# Revit family: Haworth_XSeries_LateralFile
name_source: partatom
category: Furniture Systems
revit_build: Autodesk Revit 2018 (Build: 20170223_1515(x64)
units: mm (PartAtom-declared; Revit-internal decimal feet)

## family parameters
Always vertical = Yes
Cut with Voids When Loaded = No
OmniClass Number = 23.40.70.14.64.21
OmniClass Title = Systems Furniture
Part Type = Normal
Room Calculation Point = No
Round Connector Dimension = Use Diameter
Shared = No
Work Plane-Based = No

## types (11) — shared parameters
Actual Width = 35 7/8"
Assembly Code = E2020200
Crescent Pull = No
Custom Size = No
Description = Haworth XSeries Lateral File
Ellipse Pull = No
Integral Pull = No
J Pull = No
Linear Pull = Yes
Manufacturer = Haworth
Max # of Drawers = 5
Max. Height = 63 1/2"
Max. Width = 47 7/8"
Min. Height = 27 1/2"
Min. Width = 29 7/8"
Model = JLRD
One and One Half High = No
One and One Half High Actual = No
Pull Classic = No
Pull Finish = Haworth _ Metal _ Brushed Aluminum
Radius Pull = No
Revision Number = 5
Size = Verify Final Dim. w/ Haworth
Standard Widths = 30, 36, 42 in.
Sustainability Info = https://www.haworth.com
Taper Pull = No
URL = http://www.haworth.com
URL - Product = https://www.haworth.com
Warranty = http://www.haworth.com
Width = 36"

## per-type parameters (varying)
| type | # of Drawers | Actual # of Drawers | Actual Depth | Actual Height | Cabinet Height | Drawer 3 | Drawer 4 | Drawer 5 | Drawer Height | Drawer Width | Inset Style | Proud Offset | Proud Style | Receding Door | Receding Doors_5 High Only | Second Drawer Height | Sliding Door | Sliding Doors_5 High Only | Swing Door | Swing Door Width | Swing Doors_5 High Only | Two High |
| 18d 36w 51h - Inset Style | 4 | 4 | 18" | 51 1/2" | 51 1/2" | Yes | Yes | Yes | 12 3/32" | 34 3/8" | Yes | 0" | No | No | No | 12 3/32" | No | No | No | 17 3/16" | No | No |
| 18d 36w 39h - Inset Style | 3 | 3 | 18" | 39 1/2" | 39 1/2" | Yes | No | Yes | 12 1/8" | 34 3/8" | Yes | 0" | No | No | No | 12 1/8" | No | No | No | 17 3/16" | No | No |
| 18d 36w 27h - Inset Style | 2 | 2 | 18" | 27 1/2" | 27 1/2" | No | No | Yes | 12 3/16" | 34 3/8" | Yes | 0" | No | No | No | 12 3/16" | No | No | No | 17 3/16" | No | Yes |
| 18d 36w 63h - Inset Style - Standard Drawer | 5 | 5 | 18" | 63 1/2" | 63 1/2" | Yes | Yes | Yes | 12 19/256" | 34 3/8" | Yes | 0" | No | No | No | 12 19/256" | No | No | No | 17 3/16" | No | No |
| 18d 36w 63h - Inset Style - Receding Door | 5 | 4 | 18" | 63 1/2" | 63 1/2" | Yes | Yes | No | 12 19/256" | 34 3/8" | Yes | 0" | No | Yes | Yes | 12 19/256" | No | No | No | 17 3/16" | No | No |
| 18d 36w 63h - Inset Style - Sliding Doors | 5 | 4 | 18" | 63 1/2" | 63 1/2" | Yes | Yes | No | 12 19/256" | 34 3/8" | Yes | 0" | No | No | No | 12 19/256" | Yes | Yes | No | 17 3/16" | No | No |
| 18d 36w 27h - Proud Style | 2 | 2 | 18 3/4" | 27 1/2" | 27 1/2" | No | No | Yes | 12 3/16" | 35 7/8" | No | 3/4" | Yes | No | No | 12 3/16" | No | No | No | 17 15/16" | No | Yes |
| 18d 36w 39h - Proud Style | 3 | 3 | 18 3/4" | 39 1/2" | 39 1/2" | Yes | No | Yes | 12 1/8" | 35 7/8" | No | 3/4" | Yes | No | No | 12 1/8" | No | No | No | 17 15/16" | No | No |
| 18d 36w 51h - Proud Style | 4 | 4 | 18 3/4" | 51 1/2" | 51 1/2" | Yes | Yes | Yes | 12 3/32" | 35 7/8" | No | 3/4" | Yes | No | No | 12 3/32" | No | No | No | 17 15/16" | No | No |
| 18d 36w 63h - Proud Style - Standard Drawer | 5 | 5 | 18 3/4" | 63 1/2" | 63 1/2" | Yes | Yes | Yes | 12 19/256" | 35 7/8" | No | 3/4" | Yes | No | No | 12 19/256" | No | No | No | 17 15/16" | No | No |
| 18d 36w 63h - Proud Style - Hinged Doors | 5 | 4 | 18 3/4" | 63 1/2" | 63 1/2" | Yes | Yes | No | 12 19/256" | 35 7/8" | No | 3/4" | Yes | No | No | 12 19/256" | No | No | Yes | 17 15/16" | Yes | No |

## geometry (parser evidence)
native form markers: Sweep x18
no freeform markers — native parametric forms only
